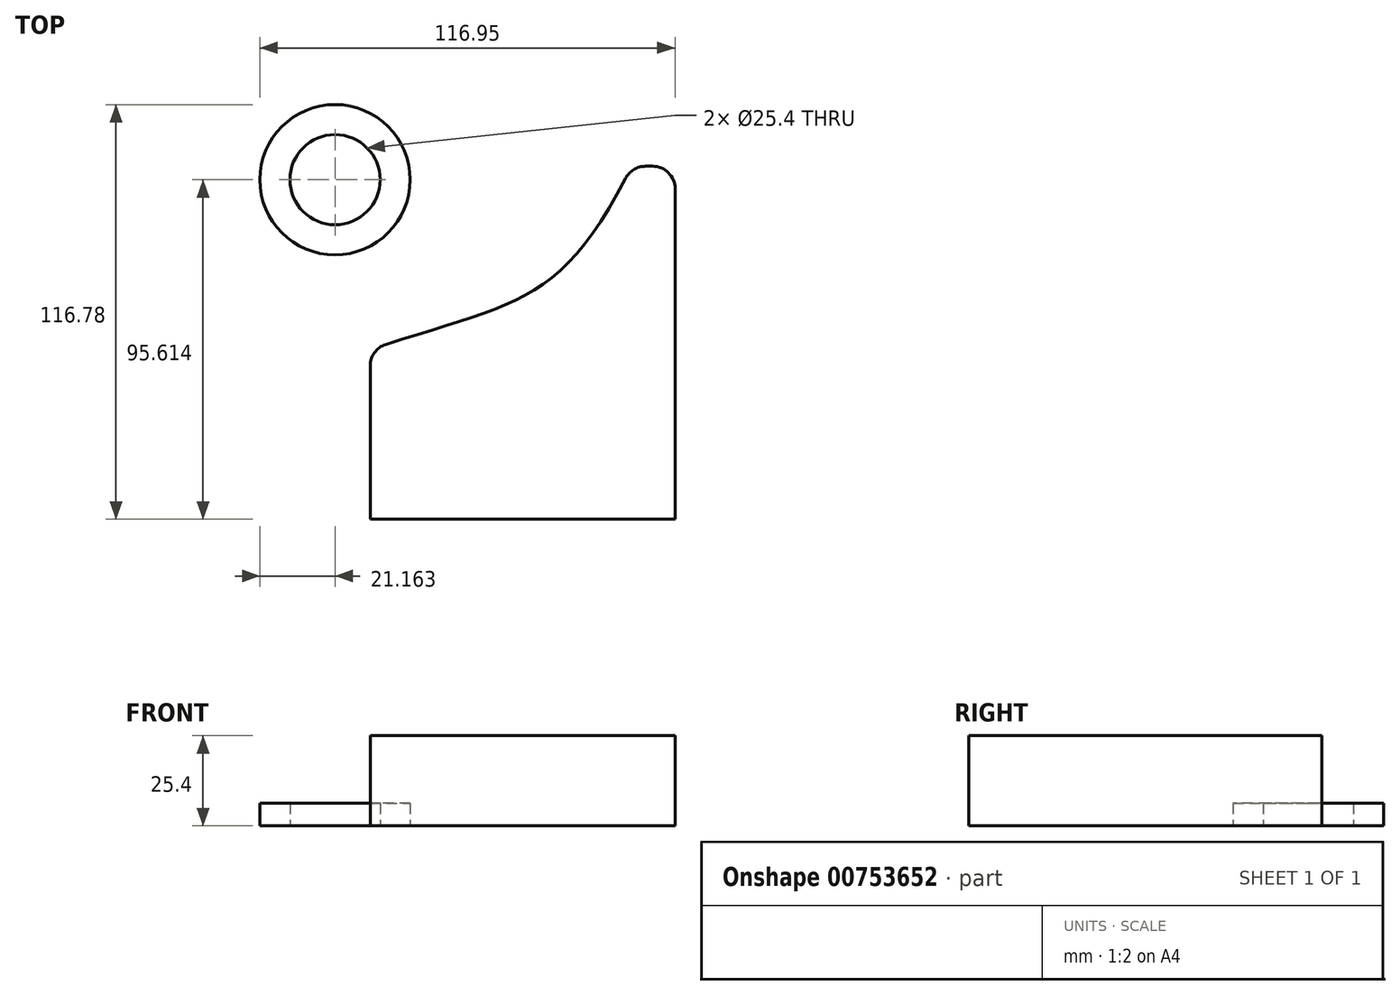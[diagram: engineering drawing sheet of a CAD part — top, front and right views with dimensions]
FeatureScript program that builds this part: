
annotation { "Feature Type Name" : "Feature", "Feature Type Description" : "" }
export const myFeature = defineFeature(function(context is Context, id is Id, definition is map)
    precondition{}
    {
        {
            var Q0;
            Q0=qCreatedBy(makeId("Top.planeOp"),FACE);
            var sketch = newSketch(context, id + "F0", { "sketchPlane" : qUnion([Q0])});
            skCircle(sketch, "E0", {"center": v(-32.86, 27.78) * mm, "radius": 21.16 * mm});
            skCircle(sketch, "E1", {"center": v(-32.86, 27.78) * mm, "radius": 12.7 * mm});
            skSolve(sketch);
        }
        {
            var Q0;
            Q0=makeQuery(id+"F0.imprint","IMPRINT",FACE,{"disambiguationData":[TD([[makeQuery(id+"F0.imprint","IMPRINT",EDGE,{"derivedFrom":sQuery(id+"F0.wireOp",EDGE,"E0")}),1.0]])]});
            extrude(context, id + "F1", {"entities" : qUnion([Q0]), "depth" : 6.35 * mm, "offsetDistance" : 25.4 * mm});
        }
        {
            var Q0;
            Q0=qCreatedBy(makeId("Top.planeOp"),FACE);
            var sketch = newSketch(context, id + "F2", { "sketchPlane" : qUnion([Q0])});
            skLineSegment(sketch, "E2.bottom", {"start": v(-22.96, -20.04) * mm, "end": v(50.7, -20.04) * mm});
            skLineSegment(sketch, "E2.top", {"start": v(-22.96, -67.83) * mm, "end": v(50.7, -67.83) * mm});
            skLineSegment(sketch, "E2.left", {"start": v(-22.96, -20.04) * mm, "end": v(-22.96, -67.83) * mm});
            skLineSegment(sketch, "E2.right", {"start": v(50.7, -20.04) * mm, "end": v(50.7, -67.83) * mm});
            skLineSegment(sketch, "E3.bottom", {"start": v(50.7, 31.57) * mm, "end": v(62.93, 31.57) * mm});
            skLineSegment(sketch, "E3.top", {"start": v(50.7, -67.83) * mm, "end": v(62.93, -67.83) * mm});
            skLineSegment(sketch, "E3.left", {"start": v(50.7, 31.57) * mm, "end": v(50.7, -67.83) * mm});
            skLineSegment(sketch, "E3.right", {"start": v(62.93, 31.57) * mm, "end": v(62.93, -67.83) * mm});
            skFitSpline(sketch, "E4", {"points": [v(50.7, 31.57) * mm, v(-22.96, -20.04) * mm], "startDerivative": vector(-59.92, -120.58) * mm, "endDerivative": vector(-122.14, -40.53) * mm});
            skSolve(sketch);
        }
        {
            var Q0;
            {var subQ0=sQuery(id+"F2.wireOp",EDGE,"E2.bottom");Q0=makeQuery(id+"F2.imprint","IMPRINT",FACE,{"disambiguationData":[TD([[makeQuery(id+"F2.imprint","IMPRINT",EDGE,{"derivedFrom":subQ0}),1.0]])]});}
            var Q1;
            {var subQ3=sQuery(id+"F2.wireOp",EDGE,"E3.bottom");Q1=makeQuery(id+"F2.imprint","IMPRINT",FACE,{"disambiguationData":[TD([[makeQuery(id+"F2.imprint","IMPRINT",EDGE,{"derivedFrom":subQ3}),-1.0]])]});}
            var Q2;
            {var subQ0=sQuery(id+"F2.wireOp",EDGE,"E2.bottom");Q2=makeQuery(id+"F2.imprint","IMPRINT",FACE,{"disambiguationData":[TD([[makeQuery(id+"F2.imprint","IMPRINT",EDGE,{"derivedFrom":subQ0}),-1.0]])]});}
            extrude(context, id + "F3", {"entities" : qUnion([Q0, Q1, Q2]), "depth" : 25.4 * mm, "offsetDistance" : 25.4 * mm});
        }
        {
            var Q0;
            Q0=makeQuery(id+"F3.opExtrude","SWEPT_EDGE",EDGE,{"disambiguationData":[OSD([sQuery(id+"F2.wireOp",EDGE,"E2.bottom"),sQuery(id+"F2.wireOp",EDGE,"E2.left"),sQuery(id+"F2.wireOp",EDGE,"E4")])]});
            var Q1;
            Q1=makeQuery(id+"F3.opExtrude","SWEPT_EDGE",EDGE,{"disambiguationData":[OSD([sQuery(id+"F2.wireOp",EDGE,"E3.bottom"),sQuery(id+"F2.wireOp",EDGE,"E3.left"),sQuery(id+"F2.wireOp",EDGE,"E4")])]});
            fillet(context, id + "F4", {"entities" : qUnion([Q0, Q1]), "radius" : 6.35 * mm, "tangentPropagation" : true, "allowEdgeOverflow" : false});
        }
        {
            var Q0;
            Q0=makeQuery(id+"F3.opExtrude","SWEPT_EDGE",EDGE,{"disambiguationData":[OSD([sQuery(id+"F2.wireOp",EDGE,"E3.bottom"),sQuery(id+"F2.wireOp",EDGE,"E3.right")])]});
            fillet(context, id + "F5", {"entities" : qUnion([Q0]), "radius" : 6.35 * mm, "tangentPropagation" : true, "allowEdgeOverflow" : false});
        }
        {
            var Q0;
            Q0=makeQuery(id+"F1.opExtrude","SWEPT_BODY",BODY,{"disambiguationData":[OSD([sQuery(id+"F0.wireOp",EDGE,"E0"),sQuery(id+"F0.wireOp",EDGE,"E1")])]});
            transform(context, id + "F6", {"entities" : qUnion([Q0]), "transformType" : TransformType.TRANSLATION_3D, "dx" : 0 * mm, "dy" : 0 * mm, "dz" : 0 * mm, "makeCopy" : true});
        }
    });
